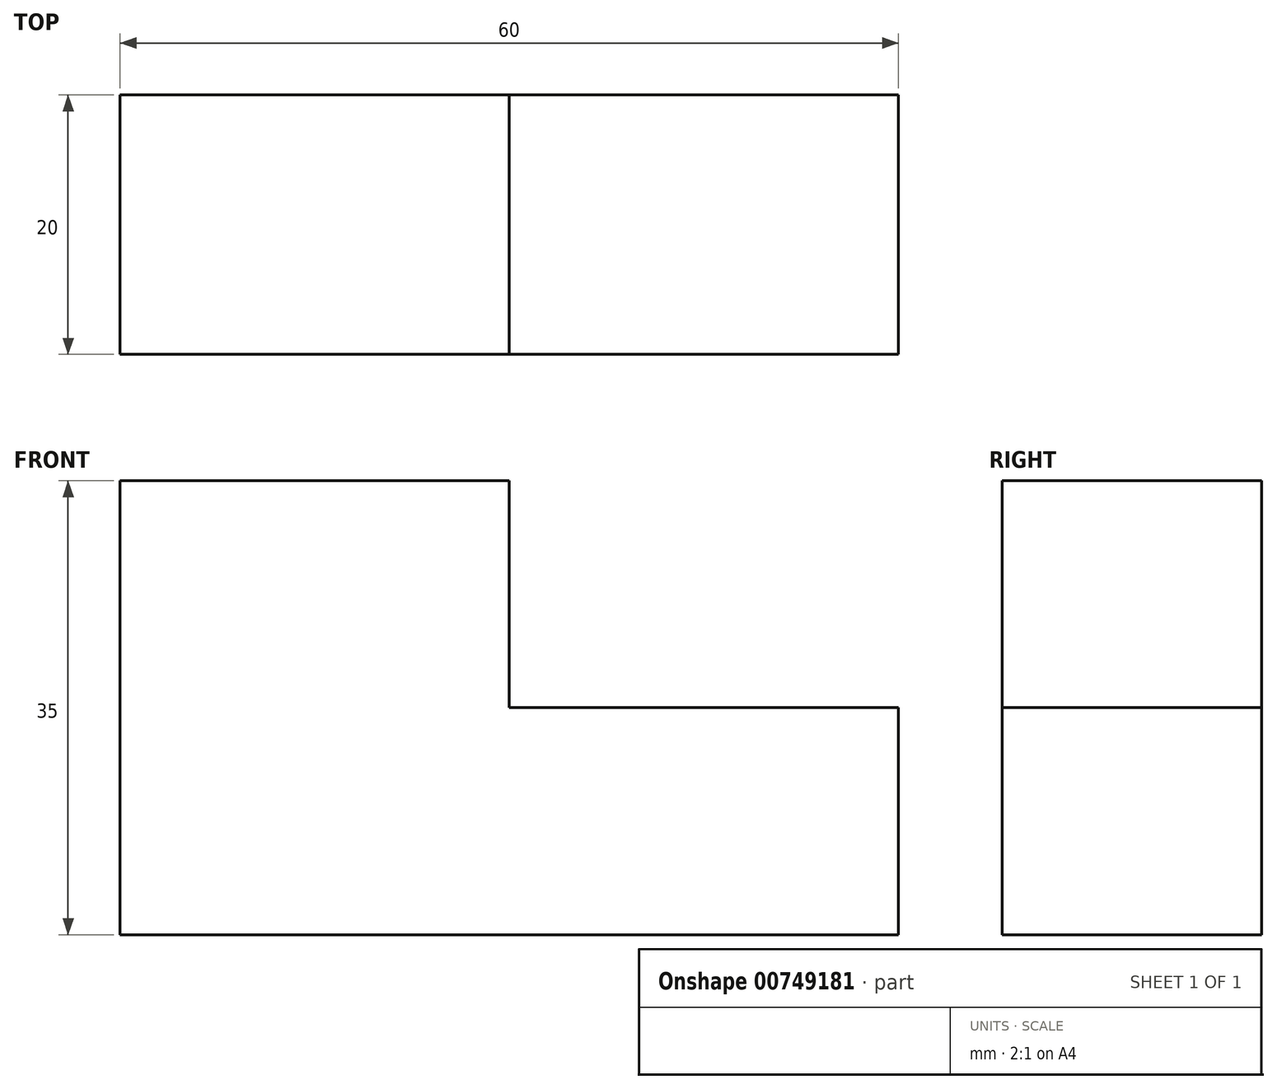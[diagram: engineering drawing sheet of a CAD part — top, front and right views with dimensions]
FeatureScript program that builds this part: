
annotation { "Feature Type Name" : "Feature", "Feature Type Description" : "" }
export const myFeature = defineFeature(function(context is Context, id is Id, definition is map)
    precondition{}
    {
        {
            var Q0;
            Q0=qCreatedBy(makeId("Top.planeOp"),FACE);
            var sketch = newSketch(context, id + "F0", { "sketchPlane" : qUnion([Q0])});
            skLineSegment(sketch, "E0.bottom", {"start": v(0, 20) * mm, "end": v(60, 20) * mm});
            skLineSegment(sketch, "E0.top", {"start": v(0, 0) * mm, "end": v(60, 0) * mm});
            skLineSegment(sketch, "E0.left", {"start": v(0, 20) * mm, "end": v(0, 0) * mm});
            skLineSegment(sketch, "E0.right", {"start": v(60, 20) * mm, "end": v(60, 0) * mm});
            skLineSegment(sketch, "E1", {"start": v(30, 20) * mm, "end": v(30, 0) * mm});
            skLineSegment(sketch, "E2", {"start": v(60, 0) * mm, "end": v(30, 0) * mm});
            skLineSegment(sketch, "E3", {"start": v(60, 20) * mm, "end": v(30, 20) * mm});
            skSolve(sketch);
        }
        {
            var Q0;
            {var subQ0=sQuery(id+"F0.wireOp",EDGE,"E0.left");Q0=makeQuery(id+"F0.imprint","IMPRINT",FACE,{"disambiguationData":[TD([[makeQuery(id+"F0.imprint","IMPRINT",EDGE,{"derivedFrom":subQ0}),1.0]])]});}
            extrude(context, id + "F1", {"entities" : qUnion([Q0]), "depth" : 35 * mm, "offsetDistance" : 25 * mm});
        }
        {
            var Q0;
            {var subQ0=sQuery(id+"F0.wireOp",EDGE,"E0.right");Q0=makeQuery(id+"F0.imprint","IMPRINT",FACE,{"disambiguationData":[TD([[makeQuery(id+"F0.imprint","IMPRINT",EDGE,{"derivedFrom":subQ0}),-1.0]])]});}
            extrude(context, id + "F2", {"entities" : qUnion([Q0]), "operationType" : NewBodyOperationType.ADD, "depth" : 17.5 * mm, "offsetDistance" : 25 * mm});
        }
    });
